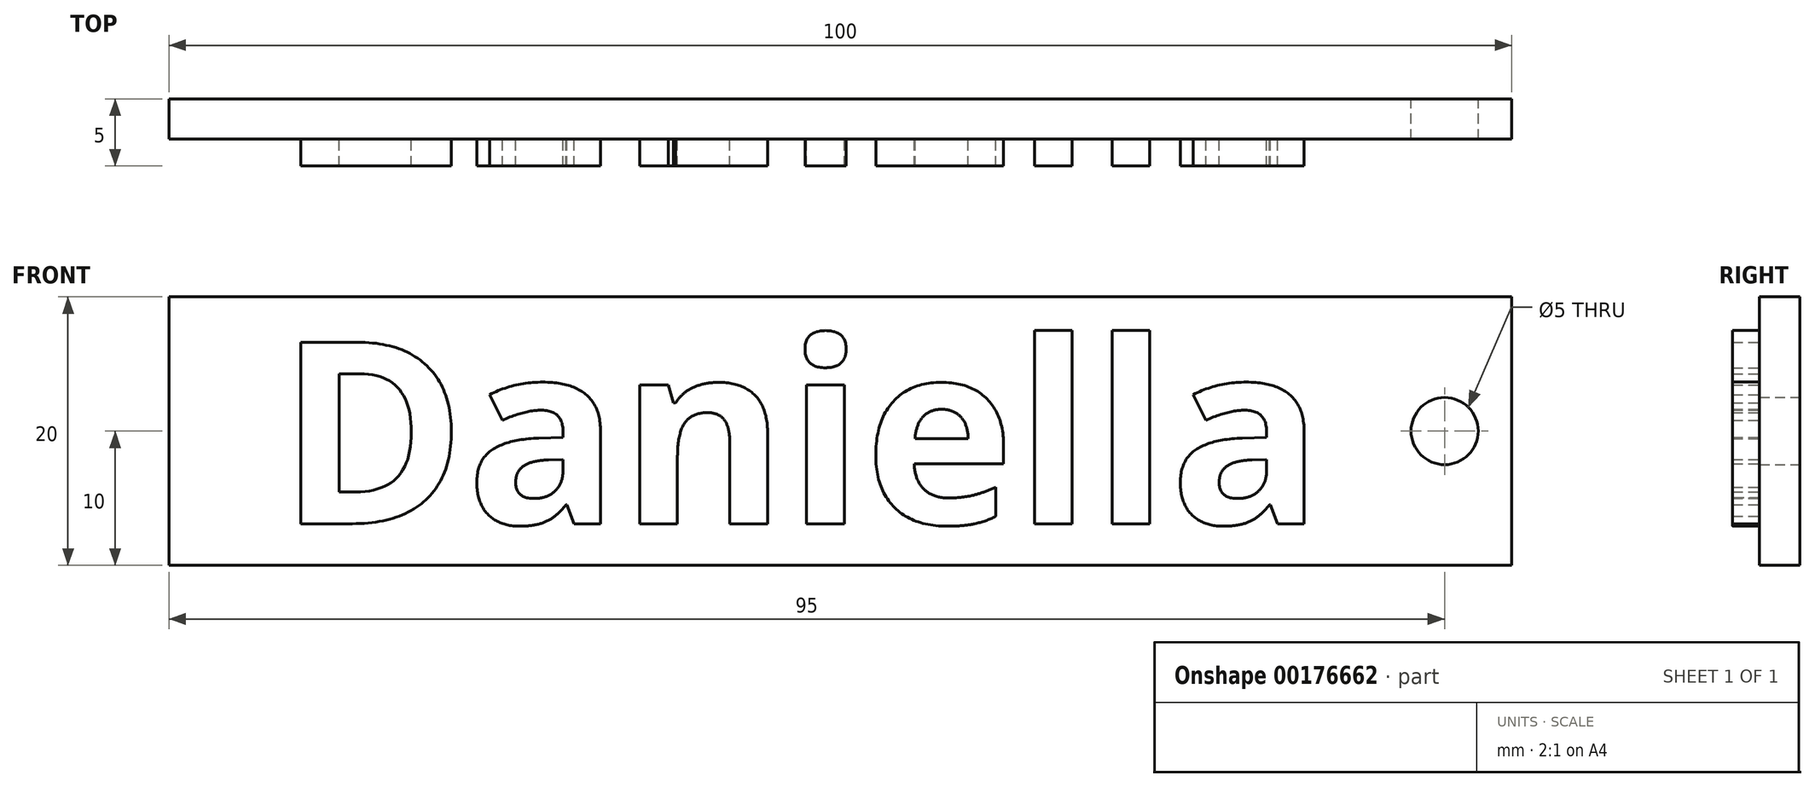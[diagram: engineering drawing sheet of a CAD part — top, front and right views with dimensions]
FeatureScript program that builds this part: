
annotation { "Feature Type Name" : "Feature", "Feature Type Description" : "" }
export const myFeature = defineFeature(function(context is Context, id is Id, definition is map)
    precondition{}
    {
        {
            var Q0;
            Q0=qCreatedBy(makeId("Front.planeOp"),FACE);
            var sketch = newSketch(context, id + "F0", { "sketchPlane" : qUnion([Q0])});
            skLineSegment(sketch, "E0.bottom", {"start": v(0, 0) * mm, "end": v(100, 0) * mm});
            skLineSegment(sketch, "E0.top", {"start": v(0, -20) * mm, "end": v(100, -20) * mm});
            skLineSegment(sketch, "E0.left", {"start": v(0, 0) * mm, "end": v(0, -20) * mm});
            skLineSegment(sketch, "E0.right", {"start": v(100, 0) * mm, "end": v(100, -20) * mm});
            skCircle(sketch, "E1", {"center": v(95, -10) * mm, "radius": 2.5 * mm});
            skSolve(sketch);
        }
        {
            var Q0;
            Q0 = qSketchRegion(id + "F0", true);
            extrude(context, id + "F1", {"entities" : qUnion([Q0]), "depth" : 3 * mm});
        }
        {
            var Q0;
            Q0=qCreatedBy(makeId("Front.planeOp"),FACE);
            var sketch = newSketch(context, id + "F2", { "sketchPlane" : qUnion([Q0])});
            skText(sketch, "E2", { "text": "Daniella", "fontName": "OpenSans-Bold.ttf"});
            const initialGuessF2  = {"E2": [0.00812, -0.0169, 1, 0, 0.01363]};
            skSetInitialGuess(sketch, initialGuessF2);
            skSolve(sketch);
        }
        {
            var Q0;
            Q0 = qSketchRegion(id + "F2", true);
            extrude(context, id + "F3", {"entities" : qUnion([Q0]), "operationType" : NewBodyOperationType.ADD, "depth" : 5 * mm});
        }
    });
